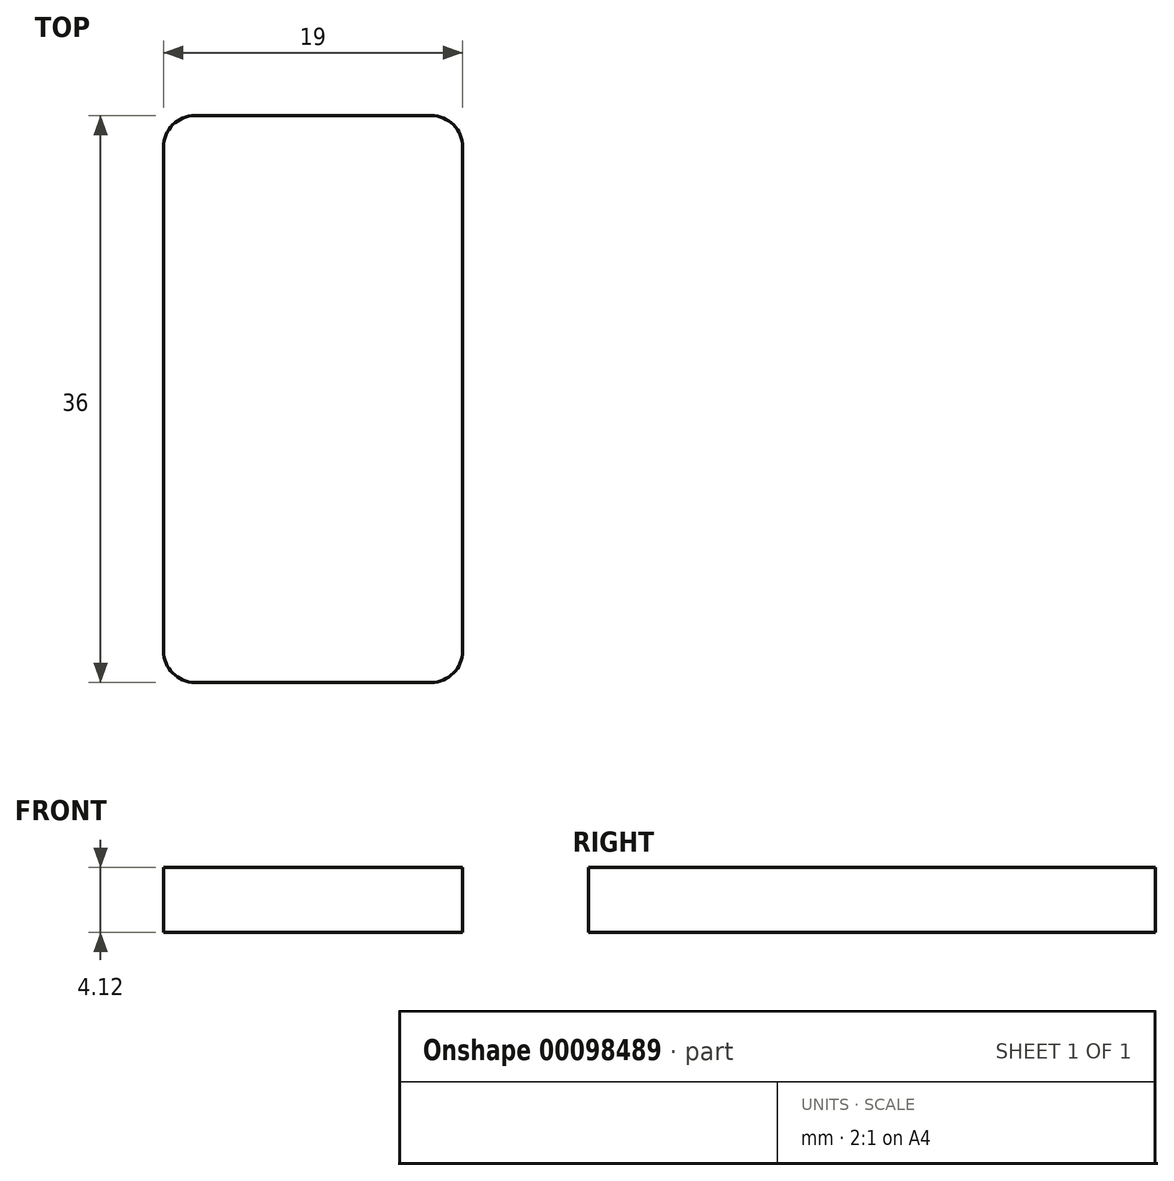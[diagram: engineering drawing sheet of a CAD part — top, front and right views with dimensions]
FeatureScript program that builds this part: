
annotation { "Feature Type Name" : "Feature", "Feature Type Description" : "" }
export const myFeature = defineFeature(function(context is Context, id is Id, definition is map)
    precondition{}
    {
        {
            var Q0;
            Q0=qCreatedBy(makeId("Top.planeOp"),FACE);
            var sketch = newSketch(context, id + "F0", { "sketchPlane" : qUnion([Q0])});
            skLineSegment(sketch, "E0.bottom", {"start": v(9.5, -18) * mm, "end": v(-9.5, -18) * mm});
            skLineSegment(sketch, "E0.top", {"start": v(9.5, 18) * mm, "end": v(-9.5, 18) * mm});
            skLineSegment(sketch, "E0.left", {"start": v(9.5, -18) * mm, "end": v(9.5, 18) * mm});
            skLineSegment(sketch, "E0.right", {"start": v(-9.5, -18) * mm, "end": v(-9.5, 18) * mm});
            skPoint(sketch, "E0.middle", {"position": v(0, 0) * mm});
            skSolve(sketch);
        }
        {
            var Q0;
            Q0=qSketchRegion(id+"F0",true);
            extrude(context, id + "F1", {"entities" : qUnion([Q0]), "depth" : 4.12 * mm});
        }
        {
            var Q0;
            Q0=makeQuery(id+"F1.opExtrude","SWEPT_EDGE",EDGE,{"disambiguationData":[OSD([sQuery(id+"F0.wireOp",EDGE,"E0.top"),sQuery(id+"F0.wireOp",EDGE,"E0.right")])]});
            var Q1;
            Q1=makeQuery(id+"F1.opExtrude","SWEPT_EDGE",EDGE,{"disambiguationData":[OSD([sQuery(id+"F0.wireOp",EDGE,"E0.top"),sQuery(id+"F0.wireOp",EDGE,"E0.left")])]});
            var Q2;
            Q2=makeQuery(id+"F1.opExtrude","SWEPT_EDGE",EDGE,{"disambiguationData":[OSD([sQuery(id+"F0.wireOp",EDGE,"E0.bottom"),sQuery(id+"F0.wireOp",EDGE,"E0.left")])]});
            var Q3;
            Q3=makeQuery(id+"F1.opExtrude","SWEPT_EDGE",EDGE,{"disambiguationData":[OSD([sQuery(id+"F0.wireOp",EDGE,"E0.bottom"),sQuery(id+"F0.wireOp",EDGE,"E0.right")])]});
            fillet(context, id + "F2", {"entities" : qUnion([Q0, Q1, Q2, Q3]), "radius" : 2 * mm, "tangentPropagation" : true, "allowEdgeOverflow" : false});
        }
    });
